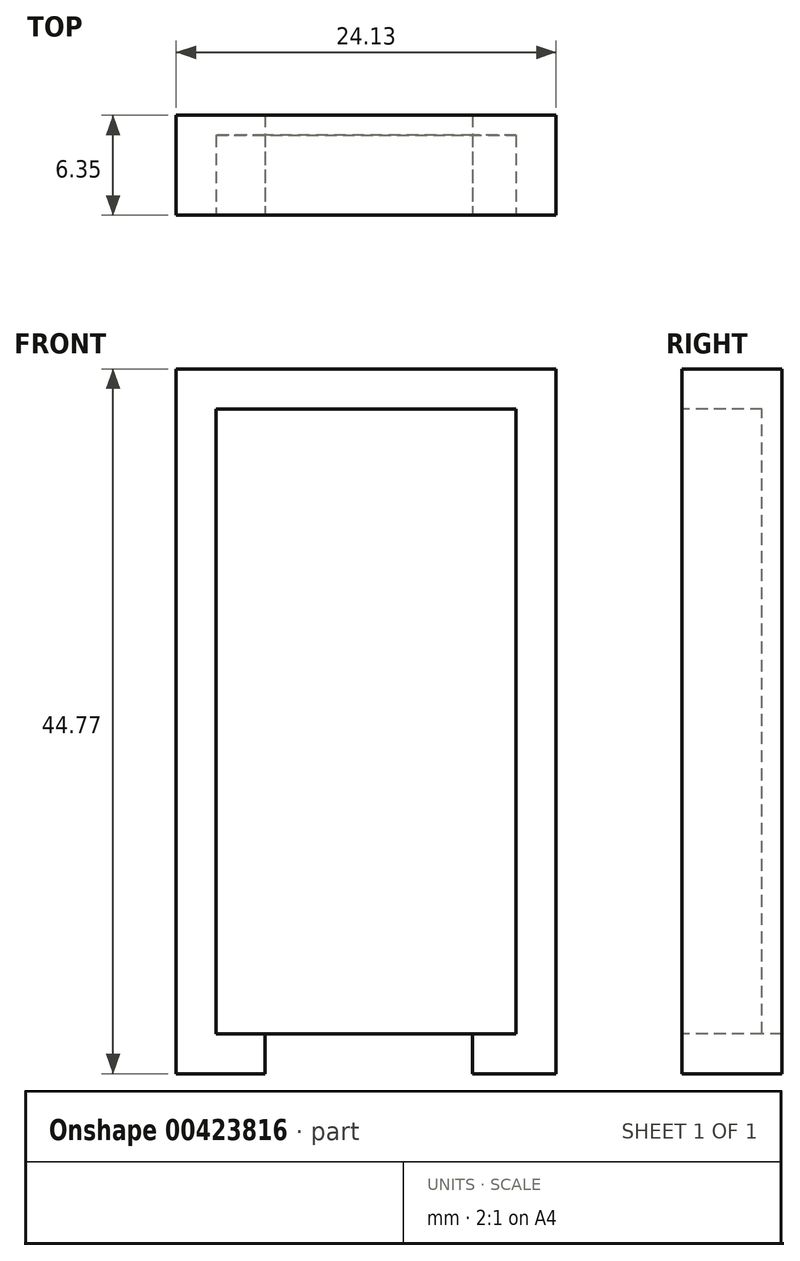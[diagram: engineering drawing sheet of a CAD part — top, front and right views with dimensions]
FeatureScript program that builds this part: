
annotation { "Feature Type Name" : "Feature", "Feature Type Description" : "" }
export const myFeature = defineFeature(function(context is Context, id is Id, definition is map)
    precondition{}
    {
        {
            var Q0;
            Q0=qCreatedBy(makeId("Front.planeOp"),FACE);
            var sketch = newSketch(context, id + "F0", { "sketchPlane" : qUnion([Q0])});
            skLineSegment(sketch, "E0.bottom", {"start": v(0, 0) * mm, "end": v(-24.13, 0) * mm});
            skLineSegment(sketch, "E0.top", {"start": v(0, 44.77) * mm, "end": v(-24.13, 44.77) * mm});
            skLineSegment(sketch, "E0.left", {"start": v(0, 0) * mm, "end": v(0, 44.77) * mm});
            skLineSegment(sketch, "E0.right", {"start": v(-24.13, 0) * mm, "end": v(-24.13, 44.77) * mm});
            skSolve(sketch);
        }
        {
            var Q0;
            Q0 = qSketchRegion(id + "F0", true);
            extrude(context, id + "F1", {"entities" : qUnion([Q0]), "depth" : 6.35 * mm});
        }
        {
            var Q0;
            Q0=makeQuery(id+"F1.opExtrude","CAP_FACE",FACE,{"disambiguationData":[OSD([sQuery(id+"F0.wireOp",EDGE,"E0.bottom"),sQuery(id+"F0.wireOp",EDGE,"E0.top"),sQuery(id+"F0.wireOp",EDGE,"E0.left"),sQuery(id+"F0.wireOp",EDGE,"E0.right")])],"isStart":false});
            var sketch = newSketch(context, id + "F2", { "sketchPlane" : qUnion([Q0])});
            skLineSegment(sketch, "E1.bottom", {"start": v(-24.13, 0) * mm, "end": v(-21.59, 0) * mm});
            skLineSegment(sketch, "E1.top", {"start": v(-24.13, 0) * mm, "end": v(-21.59, 0) * mm});
            skLineSegment(sketch, "E1.left", {"start": v(-24.13, 0) * mm, "end": v(-24.13, 0) * mm});
            skLineSegment(sketch, "E1.right", {"start": v(-21.59, 0) * mm, "end": v(-21.59, 0) * mm});
            skLineSegment(sketch, "E2.bottom", {"start": v(0, 0) * mm, "end": v(-2.54, 0) * mm});
            skLineSegment(sketch, "E2.top", {"start": v(0, 0) * mm, "end": v(-2.54, 0) * mm});
            skLineSegment(sketch, "E2.left", {"start": v(0, 0) * mm, "end": v(0, 0) * mm});
            skLineSegment(sketch, "E2.right", {"start": v(-2.54, 0) * mm, "end": v(-2.54, 0) * mm});
            skLineSegment(sketch, "E3", {"start": v(-24.13, 44.77) * mm, "end": v(-24.13, 42.23) * mm});
            skLineSegment(sketch, "E4", {"start": v(-21.59, 0) * mm, "end": v(-21.59, 2.54) * mm});
            skLineSegment(sketch, "E5", {"start": v(-21.59, 2.54) * mm, "end": v(-21.59, 42.23) * mm});
            skLineSegment(sketch, "E6", {"start": v(-21.59, 42.23) * mm, "end": v(-2.54, 42.23) * mm});
            skLineSegment(sketch, "E7", {"start": v(-2.54, 42.23) * mm, "end": v(-2.54, 2.54) * mm});
            skLineSegment(sketch, "E8", {"start": v(-2.54, 2.54) * mm, "end": v(-21.59, 2.54) * mm});
            skSolve(sketch);
        }
        {
            var Q0;
            Q0 = qSketchRegion(id + "F2", true);
            extrude(context, id + "F3", {"entities" : qUnion([Q0]), "operationType" : NewBodyOperationType.REMOVE, "oppositeDirection" : true, "depth" : 5.08 * mm});
        }
        {
            var Q0;
            Q0=makeQuery(id+"F1.opExtrude","CAP_FACE",FACE,{"disambiguationData":[OSD([sQuery(id+"F0.wireOp",EDGE,"E0.bottom"),sQuery(id+"F0.wireOp",EDGE,"E0.top"),sQuery(id+"F0.wireOp",EDGE,"E0.left"),sQuery(id+"F0.wireOp",EDGE,"E0.right")])],"isStart":false});
            var sketch = newSketch(context, id + "F4", { "sketchPlane" : qUnion([Q0])});
            skLineSegment(sketch, "E9.bottom", {"start": v(-18.48, 0) * mm, "end": v(-5.3, 0) * mm});
            skLineSegment(sketch, "E9.top", {"start": v(-18.48, 2.54) * mm, "end": v(-5.3, 2.54) * mm});
            skLineSegment(sketch, "E9.left", {"start": v(-18.48, 0) * mm, "end": v(-18.48, 2.54) * mm});
            skLineSegment(sketch, "E9.right", {"start": v(-5.3, 0) * mm, "end": v(-5.3, 2.54) * mm});
            skSolve(sketch);
        }
        {
            var Q0;
            Q0 = qSketchRegion(id + "F4", true);
            extrude(context, id + "F5", {"entities" : qUnion([Q0]), "operationType" : NewBodyOperationType.REMOVE, "oppositeDirection" : true, "depth" : 6.35 * mm});
        }
    });
